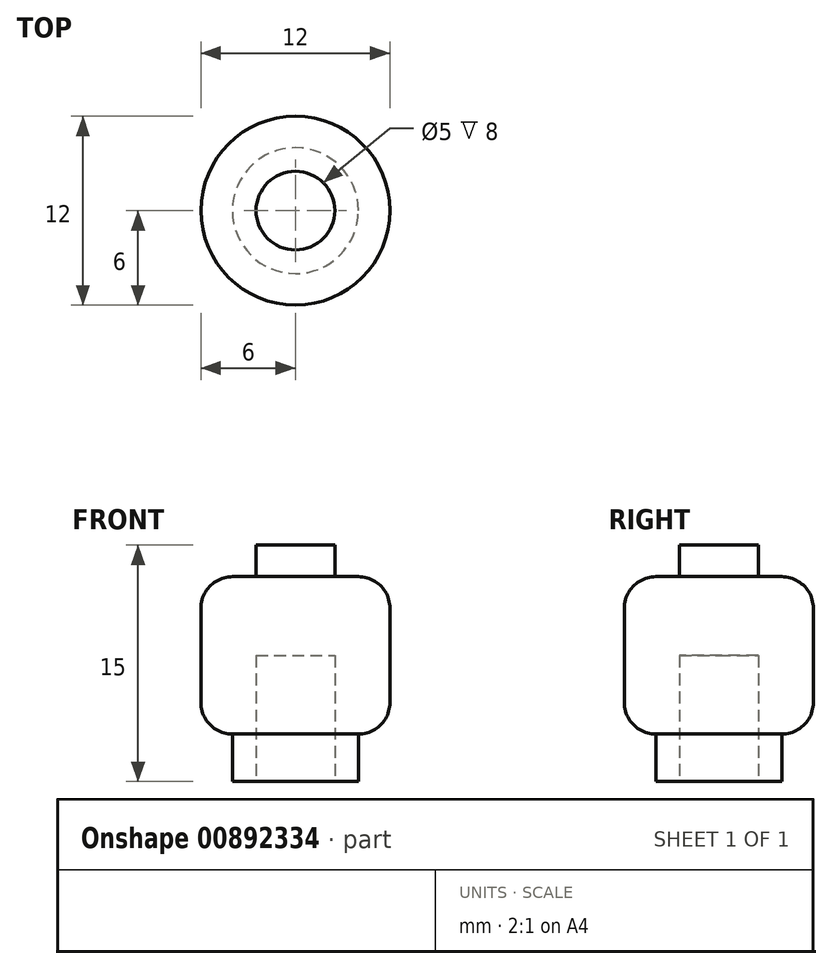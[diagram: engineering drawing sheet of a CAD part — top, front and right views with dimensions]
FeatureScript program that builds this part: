
annotation { "Feature Type Name" : "Feature", "Feature Type Description" : "" }
export const myFeature = defineFeature(function(context is Context, id is Id, definition is map)
    precondition{}
    {
        {
            var Q0;
            Q0=qCreatedBy(makeId("Top.planeOp"),FACE);
            var sketch = newSketch(context, id + "F0", { "sketchPlane" : qUnion([Q0])});
            skCircle(sketch, "E0", {"center": v(0, 0) * mm, "radius": 4 * mm});
            skSolve(sketch);
        }
        {
            var Q0;
            Q0 = qSketchRegion(id + "F0", true);
            extrude(context, id + "F1", {"entities" : qUnion([Q0]), "depth" : 3 * mm, "offsetDistance" : 25.4 * mm});
        }
        {
            var Q0;
            Q0=makeQuery(id+"F1.opExtrude","CAP_FACE",FACE,{"disambiguationData":[OSD([sQuery(id+"F0.wireOp",EDGE,"E0")])],"isStart":false});
            var sketch = newSketch(context, id + "F2", { "sketchPlane" : qUnion([Q0])});
            skCircle(sketch, "E1", {"center": v(0, 0) * mm, "radius": 6 * mm});
            skSolve(sketch);
        }
        {
            var Q0;
            Q0 = qSketchRegion(id + "F2", true);
            extrude(context, id + "F3", {"entities" : qUnion([Q0]), "operationType" : NewBodyOperationType.ADD, "depth" : 10 * mm, "offsetDistance" : 25.4 * mm});
        }
        {
            var Q0;
            Q0=makeQuery(id+"F3.opExtrude","CAP_FACE",FACE,{"disambiguationData":[OSD([sQuery(id+"F2.wireOp",EDGE,"E1")])],"isStart":false});
            var sketch = newSketch(context, id + "F4", { "sketchPlane" : qUnion([Q0])});
            skCircle(sketch, "E2", {"center": v(0, 0) * mm, "radius": 2.5 * mm});
            skSolve(sketch);
        }
        {
            var Q0;
            Q0 = qSketchRegion(id + "F4", true);
            extrude(context, id + "F5", {"entities" : qUnion([Q0]), "operationType" : NewBodyOperationType.ADD, "depth" : 2 * mm, "offsetDistance" : 25.4 * mm});
        }
        {
            var Q0;
            Q0=makeQuery(id+"F3.opExtrude","CAP_EDGE",EDGE,{"disambiguationData":[OSD([sQuery(id+"F2.wireOp",EDGE,"E1")])],"isStart":false});
            var Q1;
            Q1=makeQuery(id+"F3.opExtrude","CAP_EDGE",EDGE,{"disambiguationData":[OSD([sQuery(id+"F2.wireOp",EDGE,"E1")])],"isStart":true});
            fillet(context, id + "F6", {"entities" : qUnion([Q0, Q1]), "radius" : 2 * mm, "tangentPropagation" : true, "allowEdgeOverflow" : false});
        }
        {
            var Q0;
            Q0=makeQuery(id+"F1.opExtrude","CAP_FACE",FACE,{"disambiguationData":[OSD([sQuery(id+"F0.wireOp",EDGE,"E0")])],"isStart":true});
            var sketch = newSketch(context, id + "F7", { "sketchPlane" : qUnion([Q0])});
            skCircle(sketch, "E3", {"center": v(0, 0) * mm, "radius": 2.5 * mm});
            skSolve(sketch);
        }
        {
            var Q0;
            Q0 = qSketchRegion(id + "F7", true);
            extrude(context, id + "F8", {"entities" : qUnion([Q0]), "operationType" : NewBodyOperationType.REMOVE, "oppositeDirection" : true, "depth" : 8 * mm, "offsetDistance" : 25.4 * mm});
        }
    });
